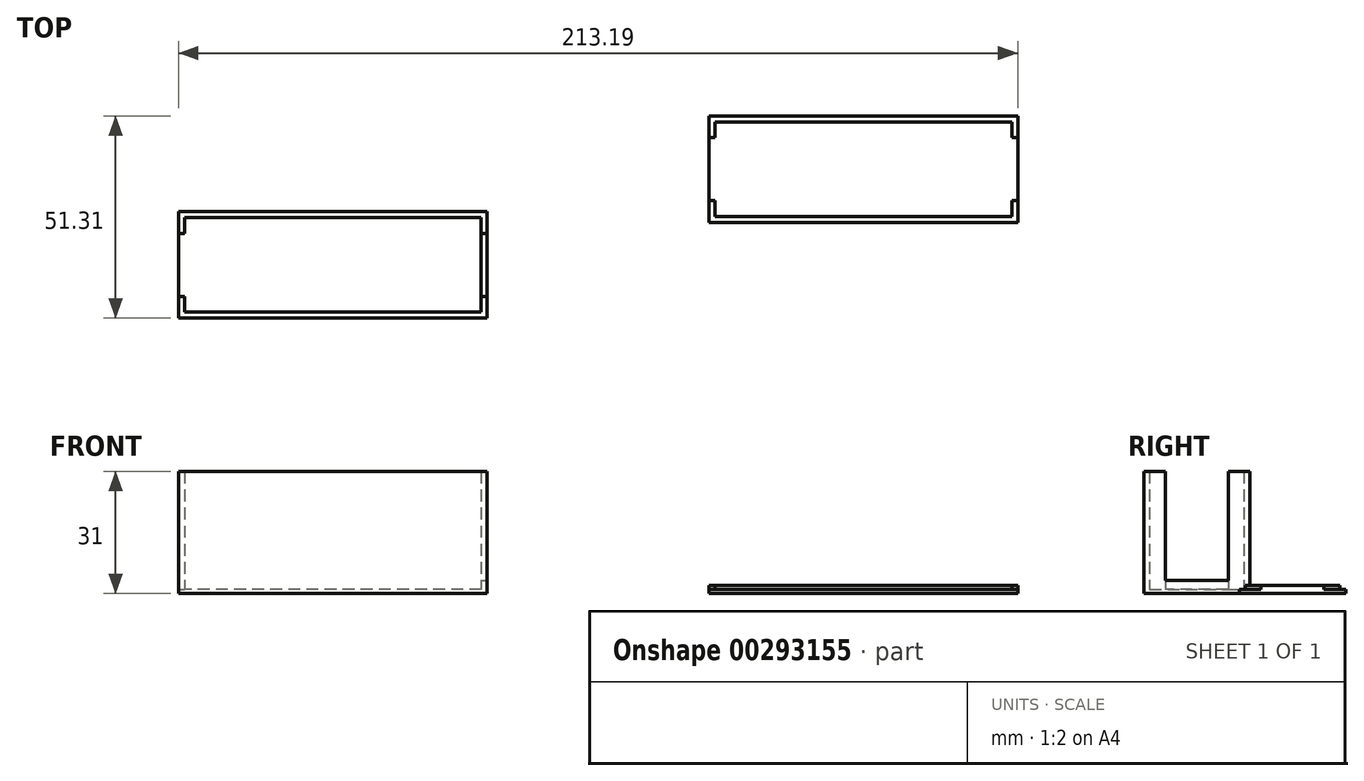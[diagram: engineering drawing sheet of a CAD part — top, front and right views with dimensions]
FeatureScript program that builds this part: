
annotation { "Feature Type Name" : "Feature", "Feature Type Description" : "" }
export const myFeature = defineFeature(function(context is Context, id is Id, definition is map)
    precondition{}
    {
        {
            var Q0;
            Q0=qCreatedBy(makeId("Top.planeOp"),FACE);
            var sketch = newSketch(context, id + "F0", { "sketchPlane" : qUnion([Q0])});
            skLineSegment(sketch, "E0.bottom", {"start": v(-51.27, -6.28) * mm, "end": v(24.13, -6.28) * mm});
            skLineSegment(sketch, "E0.top", {"start": v(-51.27, -30.28) * mm, "end": v(24.13, -30.28) * mm});
            skLineSegment(sketch, "E0.left", {"start": v(-51.27, -6.28) * mm, "end": v(-51.27, -30.28) * mm});
            skLineSegment(sketch, "E0.right", {"start": v(24.13, -6.28) * mm, "end": v(24.13, -30.28) * mm});
            skLineSegment(sketch, "E1.0", {"start": v(-52.77, -4.78) * mm, "end": v(25.63, -4.78) * mm});
            skLineSegment(sketch, "E1.1", {"start": v(-52.77, -4.78) * mm, "end": v(-52.77, -31.78) * mm});
            skLineSegment(sketch, "E1.2", {"start": v(-52.77, -31.78) * mm, "end": v(25.63, -31.78) * mm});
            skLineSegment(sketch, "E1.3", {"start": v(25.63, -4.78) * mm, "end": v(25.63, -31.78) * mm});
            skLineSegment(sketch, "E2", {"start": v(-51.27, -6.28) * mm, "end": v(-51.27, -10.28) * mm});
            skLineSegment(sketch, "E3", {"start": v(-51.27, -10.28) * mm, "end": v(-52.77, -10.28) * mm});
            skLineSegment(sketch, "E4", {"start": v(-51.27, -30.28) * mm, "end": v(-51.27, -26.28) * mm});
            skLineSegment(sketch, "E5", {"start": v(-51.27, -26.28) * mm, "end": v(-52.77, -26.28) * mm});
            skLineSegment(sketch, "E6", {"start": v(24.13, -6.28) * mm, "end": v(24.13, -10.28) * mm});
            skLineSegment(sketch, "E7", {"start": v(24.13, -10.28) * mm, "end": v(25.63, -10.28) * mm});
            skLineSegment(sketch, "E8", {"start": v(24.13, -30.28) * mm, "end": v(24.13, -26.28) * mm});
            skLineSegment(sketch, "E9", {"start": v(24.13, -26.28) * mm, "end": v(25.63, -26.28) * mm});
            skLineSegment(sketch, "E10.bottom", {"start": v(83.52, 18.03) * mm, "end": v(158.92, 18.03) * mm});
            skLineSegment(sketch, "E10.top", {"start": v(83.52, -5.97) * mm, "end": v(158.92, -5.97) * mm});
            skLineSegment(sketch, "E10.left", {"start": v(83.52, 18.03) * mm, "end": v(83.52, -5.97) * mm});
            skLineSegment(sketch, "E10.right", {"start": v(158.92, 18.03) * mm, "end": v(158.92, -5.97) * mm});
            skLineSegment(sketch, "E11.0", {"start": v(82.02, 19.53) * mm, "end": v(160.42, 19.53) * mm});
            skLineSegment(sketch, "E11.1", {"start": v(82.02, 19.53) * mm, "end": v(82.02, -7.47) * mm});
            skLineSegment(sketch, "E11.2", {"start": v(82.02, -7.47) * mm, "end": v(160.42, -7.47) * mm});
            skLineSegment(sketch, "E11.3", {"start": v(160.42, 19.53) * mm, "end": v(160.42, -7.47) * mm});
            skLineSegment(sketch, "E12", {"start": v(83.52, 18.03) * mm, "end": v(83.52, 14.03) * mm});
            skLineSegment(sketch, "E13", {"start": v(83.52, 14.03) * mm, "end": v(82.02, 14.03) * mm});
            skLineSegment(sketch, "E14", {"start": v(83.52, -5.97) * mm, "end": v(83.52, -1.97) * mm});
            skLineSegment(sketch, "E15", {"start": v(83.52, -1.97) * mm, "end": v(82.02, -1.97) * mm});
            skLineSegment(sketch, "E16", {"start": v(158.92, 18.03) * mm, "end": v(158.92, 14.03) * mm});
            skLineSegment(sketch, "E17", {"start": v(158.92, 14.03) * mm, "end": v(160.42, 14.03) * mm});
            skLineSegment(sketch, "E18", {"start": v(158.92, -5.97) * mm, "end": v(158.92, -1.97) * mm});
            skLineSegment(sketch, "E19", {"start": v(158.92, -1.97) * mm, "end": v(160.42, -1.97) * mm});
            skSolve(sketch);
        }
        {
            var Q0;
            Q0=makeQuery(id+"F0.imprint","IMPRINT",FACE,{"disambiguationData":[TD([[makeQuery(id+"F0.imprint","IMPRINT",EDGE,{"derivedFrom":sQuery(id+"F0.wireOp",EDGE,"E0.top")}),-1.0]])]});
            var Q1;
            Q1=makeQuery(id+"F0.imprint","IMPRINT",FACE,{"disambiguationData":[TD([[makeQuery(id+"F0.imprint","IMPRINT",EDGE,{"derivedFrom":sQuery(id+"F0.wireOp",EDGE,"E0.bottom")}),1.0]])]});
            var Q2;
            Q2=makeQuery(id+"F0.imprint","IMPRINT",FACE,{"disambiguationData":[TD([[makeQuery(id+"F0.imprint","IMPRINT",EDGE,{"derivedFrom":sQuery(id+"F0.wireOp",EDGE,"E0.bottom")}),-1.0]])]});
            var Q3;
            Q3=makeQuery(id+"F0.imprint","IMPRINT",FACE,{"disambiguationData":[TD([[makeQuery(id+"F0.imprint","IMPRINT",EDGE,{"derivedFrom":sQuery(id+"F0.wireOp",EDGE,"E0.left")}),-1.0]])]});
            var Q4;
            Q4=makeQuery(id+"F0.imprint","IMPRINT",FACE,{"disambiguationData":[TD([[makeQuery(id+"F0.imprint","IMPRINT",EDGE,{"derivedFrom":sQuery(id+"F0.wireOp",EDGE,"E0.right")}),1.0]])]});
            extrude(context, id + "F1", {"entities" : qUnion([Q0, Q1, Q2, Q3, Q4]), "depth" : 1 * mm});
        }
        {
            var Q0;
            Q0=makeQuery(id+"F0.imprint","IMPRINT",FACE,{"disambiguationData":[TD([[makeQuery(id+"F0.imprint","IMPRINT",EDGE,{"derivedFrom":sQuery(id+"F0.wireOp",EDGE,"E0.bottom")}),1.0]])]});
            var Q1;
            Q1=makeQuery(id+"F0.imprint","IMPRINT",FACE,{"disambiguationData":[TD([[makeQuery(id+"F0.imprint","IMPRINT",EDGE,{"derivedFrom":sQuery(id+"F0.wireOp",EDGE,"E0.top")}),-1.0]])]});
            extrude(context, id + "F2", {"entities" : qUnion([Q0, Q1]), "operationType" : NewBodyOperationType.ADD, "depth" : 31 * mm});
        }
        {
            var Q0;
            Q0=makeQuery(id+"F0.imprint","IMPRINT",FACE,{"disambiguationData":[TD([[makeQuery(id+"F0.imprint","IMPRINT",EDGE,{"derivedFrom":sQuery(id+"F0.wireOp",EDGE,"E0.right")}),1.0]])]});
            extrude(context, id + "F3", {"entities" : qUnion([Q0]), "operationType" : NewBodyOperationType.ADD, "depth" : 3.3 * mm});
        }
        {
            var Q0;
            Q0=makeQuery(id+"F0.imprint","IMPRINT",FACE,{"disambiguationData":[TD([[makeQuery(id+"F0.imprint","IMPRINT",EDGE,{"derivedFrom":sQuery(id+"F0.wireOp",EDGE,"E10.bottom")}),-1.0]])]});
            var Q1;
            Q1=makeQuery(id+"F0.imprint","IMPRINT",FACE,{"disambiguationData":[TD([[makeQuery(id+"F0.imprint","IMPRINT",EDGE,{"derivedFrom":sQuery(id+"F0.wireOp",EDGE,"E10.bottom")}),1.0]])]});
            var Q2;
            Q2=makeQuery(id+"F0.imprint","IMPRINT",FACE,{"disambiguationData":[TD([[makeQuery(id+"F0.imprint","IMPRINT",EDGE,{"derivedFrom":sQuery(id+"F0.wireOp",EDGE,"E10.left")}),-1.0]])]});
            var Q3;
            Q3=makeQuery(id+"F0.imprint","IMPRINT",FACE,{"disambiguationData":[TD([[makeQuery(id+"F0.imprint","IMPRINT",EDGE,{"derivedFrom":sQuery(id+"F0.wireOp",EDGE,"E10.top")}),-1.0]])]});
            var Q4;
            Q4=makeQuery(id+"F0.imprint","IMPRINT",FACE,{"disambiguationData":[TD([[makeQuery(id+"F0.imprint","IMPRINT",EDGE,{"derivedFrom":sQuery(id+"F0.wireOp",EDGE,"E10.right")}),1.0]])]});
            extrude(context, id + "F4", {"entities" : qUnion([Q0, Q1, Q2, Q3, Q4]), "depth" : 1 * mm});
        }
        {
            var Q0;
            Q0=makeQuery(id+"F0.imprint","IMPRINT",FACE,{"disambiguationData":[TD([[makeQuery(id+"F0.imprint","IMPRINT",EDGE,{"derivedFrom":sQuery(id+"F0.wireOp",EDGE,"E10.bottom")}),-1.0]])]});
            var Q1;
            Q1=makeQuery(id+"F0.imprint","IMPRINT",FACE,{"disambiguationData":[TD([[makeQuery(id+"F0.imprint","IMPRINT",EDGE,{"derivedFrom":sQuery(id+"F0.wireOp",EDGE,"E10.left")}),-1.0]])]});
            var Q2;
            Q2=makeQuery(id+"F0.imprint","IMPRINT",FACE,{"disambiguationData":[TD([[makeQuery(id+"F0.imprint","IMPRINT",EDGE,{"derivedFrom":sQuery(id+"F0.wireOp",EDGE,"E10.right")}),1.0]])]});
            extrude(context, id + "F5", {"entities" : qUnion([Q0, Q1, Q2]), "operationType" : NewBodyOperationType.ADD, "depth" : 2 * mm});
        }
    });
